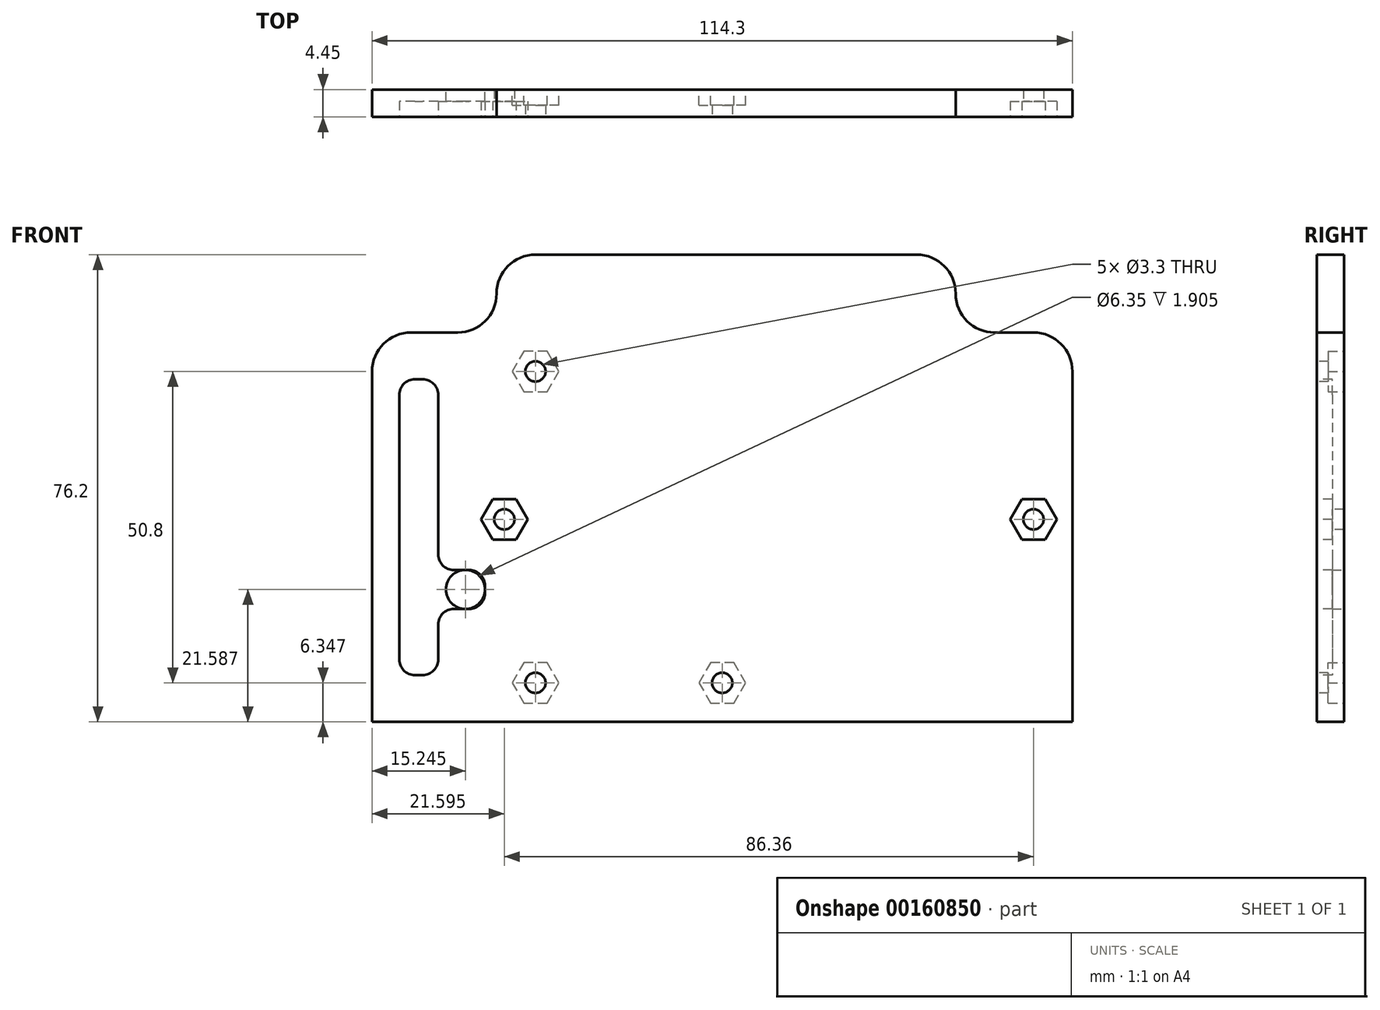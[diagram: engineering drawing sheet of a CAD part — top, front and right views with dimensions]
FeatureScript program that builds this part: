
annotation { "Feature Type Name" : "Feature", "Feature Type Description" : "" }
export const myFeature = defineFeature(function(context is Context, id is Id, definition is map)
    precondition{}
    {
        {
            var Q0;
            Q0=qCreatedBy(makeId("Front.planeOp"),FACE);
            var sketch = newSketch(context, id + "F0", { "sketchPlane" : qUnion([Q0])});
            skLineSegment(sketch, "E0.bottom", {"start": v(-28.43, 40.82) * mm, "end": v(33.8, 40.82) * mm});
            skLineSegment(sketch, "E0.top", {"start": v(-55.1, -35.38) * mm, "end": v(59.2, -35.38) * mm});
            skLineSegment(sketch, "E0.left", {"start": v(-55.1, 21.77) * mm, "end": v(-55.1, -35.38) * mm});
            skLineSegment(sketch, "E0.right", {"start": v(59.2, 21.77) * mm, "end": v(59.2, -35.38) * mm});
            skLineSegment(sketch, "E1.top", {"start": v(-48.75, 28.12) * mm, "end": v(-41.13, 28.12) * mm});
            skLineSegment(sketch, "E1.right", {"start": v(-34.78, 34.47) * mm, "end": v(-34.78, 34.47) * mm});
            skPoint(sketch, "E2.visualSharp", {"position": v(-55.1, 28.12) * mm});
            skArc(sketch, "E2.filletArc", {"start": v(-48.75, 28.12) * mm, "mid": v(-53.24, 26.26) * mm, "end": v(-55.1, 21.77) * mm});
            skPoint(sketch, "E3.visualSharp", {"position": v(-34.78, 40.82) * mm});
            skArc(sketch, "E3.filletArc", {"start": v(-28.43, 40.82) * mm, "mid": v(-32.92, 38.96) * mm, "end": v(-34.78, 34.47) * mm});
            skPoint(sketch, "E4.visualSharp", {"position": v(59.2, 40.82) * mm});
            skLineSegment(sketch, "E5.top", {"start": v(46.5, 28.12) * mm, "end": v(52.85, 28.12) * mm});
            skLineSegment(sketch, "E5.left", {"start": v(40.15, 34.47) * mm, "end": v(40.15, 34.47) * mm});
            skPoint(sketch, "E6.visualSharp", {"position": v(40.15, 28.12) * mm});
            skArc(sketch, "E6.filletArc", {"start": v(40.15, 34.47) * mm, "mid": v(42.01, 29.98) * mm, "end": v(46.5, 28.12) * mm});
            skPoint(sketch, "E7.visualSharp", {"position": v(40.15, 40.82) * mm});
            skArc(sketch, "E7.filletArc", {"start": v(40.15, 34.47) * mm, "mid": v(38.3, 38.96) * mm, "end": v(33.8, 40.82) * mm});
            skPoint(sketch, "E8.visualSharp", {"position": v(59.2, 28.12) * mm});
            skArc(sketch, "E8.filletArc", {"start": v(59.2, 21.77) * mm, "mid": v(57.34, 26.26) * mm, "end": v(52.85, 28.12) * mm});
            skPoint(sketch, "E9.visualSharp", {"position": v(-34.78, 28.12) * mm});
            skArc(sketch, "E9.filletArc", {"start": v(-41.13, 28.12) * mm, "mid": v(-36.64, 29.98) * mm, "end": v(-34.78, 34.47) * mm});
            skSolve(sketch);
        }
        {
            var Q0;
            Q0 = qSketchRegion(id + "F0", true);
            extrude(context, id + "F1", {"entities" : qUnion([Q0]), "depth" : 4.44 * mm});
        }
        {
            var Q0;
            Q0=makeQuery(id+"F1.opExtrude","CAP_FACE",FACE,{"disambiguationData":[OSD([sQuery(id+"F0.wireOp",EDGE,"E0.bottom"),sQuery(id+"F0.wireOp",EDGE,"E0.top"),sQuery(id+"F0.wireOp",EDGE,"E0.left"),sQuery(id+"F0.wireOp",EDGE,"E0.right"),sQuery(id+"F0.wireOp",EDGE,"E1.top"),sQuery(id+"F0.wireOp",EDGE,"E1.right"),sQuery(id+"F0.wireOp",EDGE,"E2.filletArc"),sQuery(id+"F0.wireOp",EDGE,"E3.filletArc"),sQuery(id+"F0.wireOp",EDGE,"E4.filletArc")])],"isStart":false});
            var sketch = newSketch(context, id + "F2", { "sketchPlane" : qUnion([Q0])});
            skCircle(sketch, "E10", {"center": v(-28.43, -29.03) * mm, "radius": 1.65 * mm});
            skCircle(sketch, "E11", {"center": v(2.05, -29.03) * mm, "radius": 1.65 * mm});
            skCircle(sketch, "E12", {"center": v(-28.43, 21.77) * mm, "radius": 1.65 * mm});
            skSolve(sketch);
        }
        {
            var Q0;
            Q0 = qSketchRegion(id + "F2", true);
            extrude(context, id + "F3", {"entities" : qUnion([Q0]), "operationType" : NewBodyOperationType.REMOVE, "endBound" : BoundingType.THROUGH_ALL, "oppositeDirection" : true, "depth" : 25.4 * mm});
        }
        {
            var Q0;
            Q0=makeQuery(id+"F1.opExtrude","CAP_FACE",FACE,{"disambiguationData":[OSD([sQuery(id+"F0.wireOp",EDGE,"E0.bottom"),sQuery(id+"F0.wireOp",EDGE,"E0.top"),sQuery(id+"F0.wireOp",EDGE,"E0.left"),sQuery(id+"F0.wireOp",EDGE,"E0.right"),sQuery(id+"F0.wireOp",EDGE,"E1.top"),sQuery(id+"F0.wireOp",EDGE,"E1.right"),sQuery(id+"F0.wireOp",EDGE,"E2.filletArc"),sQuery(id+"F0.wireOp",EDGE,"E3.filletArc"),sQuery(id+"F0.wireOp",EDGE,"E4.filletArc")])],"isStart":false});
            var sketch = newSketch(context, id + "F4", { "sketchPlane" : qUnion([Q0])});
            skCircle(sketch, "E13", {"center": v(-33.5, -2.36) * mm, "radius": 1.65 * mm});
            skCircle(sketch, "E14", {"center": v(52.85, -2.36) * mm, "radius": 1.65 * mm});
            skSolve(sketch);
        }
        {
            var Q0;
            Q0 = qSketchRegion(id + "F4", true);
            extrude(context, id + "F5", {"entities" : qUnion([Q0]), "operationType" : NewBodyOperationType.REMOVE, "endBound" : BoundingType.THROUGH_ALL, "oppositeDirection" : true, "depth" : 25.4 * mm});
        }
        {
            var Q0;
            Q0=makeQuery(id+"F1.opExtrude","CAP_FACE",FACE,{"disambiguationData":[OSD([sQuery(id+"F0.wireOp",EDGE,"E0.bottom"),sQuery(id+"F0.wireOp",EDGE,"E0.top"),sQuery(id+"F0.wireOp",EDGE,"E0.left"),sQuery(id+"F0.wireOp",EDGE,"E0.right"),sQuery(id+"F0.wireOp",EDGE,"E1.top"),sQuery(id+"F0.wireOp",EDGE,"E1.right"),sQuery(id+"F0.wireOp",EDGE,"E2.filletArc"),sQuery(id+"F0.wireOp",EDGE,"E3.filletArc"),sQuery(id+"F0.wireOp",EDGE,"E4.filletArc")])],"isStart":false});
            var sketch = newSketch(context, id + "F6", { "sketchPlane" : qUnion([Q0])});
            skCircle(sketch, "E15.cCircle", {"center": v(-33.5, -2.36) * mm, "radius": 3.81 * mm, "construction": true});
            skLineSegment(sketch, "E15.0", {"start": v(-31.6, 0.94) * mm, "end": v(-29.7, -2.36) * mm});
            skLineSegment(sketch, "E15.1", {"start": v(-29.7, -2.36) * mm, "end": v(-31.6, -5.66) * mm});
            skLineSegment(sketch, "E15.2", {"start": v(-31.6, -5.66) * mm, "end": v(-35.41, -5.66) * mm});
            skLineSegment(sketch, "E15.3", {"start": v(-35.41, -5.66) * mm, "end": v(-37.32, -2.36) * mm});
            skLineSegment(sketch, "E15.4", {"start": v(-37.32, -2.36) * mm, "end": v(-35.41, 0.94) * mm});
            skLineSegment(sketch, "E15.5", {"start": v(-35.41, 0.94) * mm, "end": v(-31.6, 0.94) * mm});
            skCircle(sketch, "E16.cCircle", {"center": v(52.85, -2.36) * mm, "radius": 3.81 * mm, "construction": true});
            skLineSegment(sketch, "E16.0", {"start": v(50.95, 0.94) * mm, "end": v(54.76, 0.94) * mm});
            skLineSegment(sketch, "E16.1", {"start": v(54.76, 0.94) * mm, "end": v(56.66, -2.36) * mm});
            skLineSegment(sketch, "E16.2", {"start": v(56.66, -2.36) * mm, "end": v(54.76, -5.66) * mm});
            skLineSegment(sketch, "E16.3", {"start": v(54.76, -5.66) * mm, "end": v(50.95, -5.66) * mm});
            skLineSegment(sketch, "E16.4", {"start": v(50.95, -5.66) * mm, "end": v(49.04, -2.36) * mm});
            skLineSegment(sketch, "E16.5", {"start": v(49.04, -2.36) * mm, "end": v(50.95, 0.94) * mm});
            skSolve(sketch);
        }
        {
            var Q0;
            Q0 = qSketchRegion(id + "F6", true);
            extrude(context, id + "F7", {"entities" : qUnion([Q0]), "operationType" : NewBodyOperationType.REMOVE, "oppositeDirection" : true, "depth" : 2.54 * mm});
        }
        {
            var Q0;
            Q0=makeQuery(id+"F1.opExtrude","CAP_FACE",FACE,{"disambiguationData":[OSD([sQuery(id+"F0.wireOp",EDGE,"E0.bottom"),sQuery(id+"F0.wireOp",EDGE,"E0.top"),sQuery(id+"F0.wireOp",EDGE,"E0.left"),sQuery(id+"F0.wireOp",EDGE,"E0.right"),sQuery(id+"F0.wireOp",EDGE,"E1.top"),sQuery(id+"F0.wireOp",EDGE,"E1.right"),sQuery(id+"F0.wireOp",EDGE,"E2.filletArc"),sQuery(id+"F0.wireOp",EDGE,"E3.filletArc"),sQuery(id+"F0.wireOp",EDGE,"E4.filletArc")])],"isStart":true});
            var sketch = newSketch(context, id + "F8", { "sketchPlane" : qUnion([Q0])});
            skCircle(sketch, "E17.cCircle", {"center": v(28.43, 21.77) * mm, "radius": 3.81 * mm, "construction": true});
            skLineSegment(sketch, "E17.0", {"start": v(32.24, 21.77) * mm, "end": v(30.33, 18.47) * mm});
            skLineSegment(sketch, "E17.1", {"start": v(30.33, 18.47) * mm, "end": v(26.52, 18.47) * mm});
            skLineSegment(sketch, "E17.2", {"start": v(26.52, 18.47) * mm, "end": v(24.62, 21.77) * mm});
            skLineSegment(sketch, "E17.3", {"start": v(24.62, 21.77) * mm, "end": v(26.52, 25.07) * mm});
            skLineSegment(sketch, "E17.4", {"start": v(26.52, 25.07) * mm, "end": v(30.33, 25.07) * mm});
            skLineSegment(sketch, "E17.5", {"start": v(30.33, 25.07) * mm, "end": v(32.24, 21.77) * mm});
            skCircle(sketch, "E18.cCircle", {"center": v(28.43, -29.03) * mm, "radius": 3.8 * mm, "construction": true});
            skLineSegment(sketch, "E18.0", {"start": v(30.33, -25.73) * mm, "end": v(32.24, -29.03) * mm});
            skLineSegment(sketch, "E18.1", {"start": v(32.24, -29.03) * mm, "end": v(30.33, -32.33) * mm});
            skLineSegment(sketch, "E18.2", {"start": v(30.33, -32.33) * mm, "end": v(26.52, -32.33) * mm});
            skLineSegment(sketch, "E18.3", {"start": v(26.52, -32.33) * mm, "end": v(24.62, -29.03) * mm});
            skLineSegment(sketch, "E18.4", {"start": v(24.62, -29.03) * mm, "end": v(26.52, -25.73) * mm});
            skLineSegment(sketch, "E18.5", {"start": v(26.52, -25.73) * mm, "end": v(30.33, -25.73) * mm});
            skCircle(sketch, "E19.cCircle", {"center": v(-2.05, -29.03) * mm, "radius": 3.8 * mm, "construction": true});
            skLineSegment(sketch, "E19.0", {"start": v(-3.96, -25.73) * mm, "end": v(-0.15, -25.73) * mm});
            skLineSegment(sketch, "E19.1", {"start": v(-0.15, -25.73) * mm, "end": v(1.76, -29.03) * mm});
            skLineSegment(sketch, "E19.2", {"start": v(1.76, -29.03) * mm, "end": v(-0.15, -32.33) * mm});
            skLineSegment(sketch, "E19.3", {"start": v(-0.15, -32.33) * mm, "end": v(-3.96, -32.33) * mm});
            skLineSegment(sketch, "E19.4", {"start": v(-3.96, -32.33) * mm, "end": v(-5.86, -29.03) * mm});
            skLineSegment(sketch, "E19.5", {"start": v(-5.86, -29.03) * mm, "end": v(-3.96, -25.73) * mm});
            skSolve(sketch);
        }
        {
            var Q0;
            Q0 = qSketchRegion(id + "F8", true);
            extrude(context, id + "F9", {"entities" : qUnion([Q0]), "operationType" : NewBodyOperationType.REMOVE, "oppositeDirection" : true, "depth" : 2.54 * mm});
        }
        {
            var Q0;
            Q0=makeQuery(id+"F1.opExtrude","CAP_FACE",FACE,{"disambiguationData":[OSD([sQuery(id+"F0.wireOp",EDGE,"E0.bottom"),sQuery(id+"F0.wireOp",EDGE,"E0.top"),sQuery(id+"F0.wireOp",EDGE,"E0.left"),sQuery(id+"F0.wireOp",EDGE,"E0.right"),sQuery(id+"F0.wireOp",EDGE,"E1.top"),sQuery(id+"F0.wireOp",EDGE,"E1.right"),sQuery(id+"F0.wireOp",EDGE,"E2.filletArc"),sQuery(id+"F0.wireOp",EDGE,"E3.filletArc"),sQuery(id+"F0.wireOp",EDGE,"E4.filletArc")])],"isStart":true});
            var sketch = newSketch(context, id + "F10", { "sketchPlane" : qUnion([Q0])});
            skCircle(sketch, "E20", {"center": v(39.86, -13.8) * mm, "radius": 3.18 * mm});
            skSolve(sketch);
        }
        {
            var Q0;
            Q0 = qSketchRegion(id + "F10", true);
            extrude(context, id + "F11", {"entities" : qUnion([Q0]), "operationType" : NewBodyOperationType.REMOVE, "endBound" : BoundingType.THROUGH_ALL, "oppositeDirection" : true, "depth" : 25.4 * mm});
        }
        {
            var Q0;
            Q0=makeQuery(id+"F1.opExtrude","CAP_FACE",FACE,{"disambiguationData":[OSD([sQuery(id+"F0.wireOp",EDGE,"E0.bottom"),sQuery(id+"F0.wireOp",EDGE,"E0.top"),sQuery(id+"F0.wireOp",EDGE,"E0.left"),sQuery(id+"F0.wireOp",EDGE,"E0.right"),sQuery(id+"F0.wireOp",EDGE,"E1.top"),sQuery(id+"F0.wireOp",EDGE,"E1.right"),sQuery(id+"F0.wireOp",EDGE,"E2.filletArc"),sQuery(id+"F0.wireOp",EDGE,"E3.filletArc"),sQuery(id+"F0.wireOp",EDGE,"E4.filletArc")])],"isStart":false});
            var sketch = newSketch(context, id + "F12", { "sketchPlane" : qUnion([Q0])});
            skLineSegment(sketch, "E21.bottom", {"start": v(-48.11, 20.5) * mm, "end": v(-46.84, 20.5) * mm});
            skLineSegment(sketch, "E21.top", {"start": v(-48.11, -27.76) * mm, "end": v(-46.84, -27.76) * mm});
            skLineSegment(sketch, "E21.left", {"start": v(-50.65, 17.96) * mm, "end": v(-50.65, -25.22) * mm});
            skLineSegment(sketch, "E21.right", {"start": v(-44.3, 17.96) * mm, "end": v(-44.3, -8.08) * mm});
            skPoint(sketch, "E22.visualSharp", {"position": v(-50.65, 20.5) * mm});
            skArc(sketch, "E22.filletArc", {"start": v(-48.11, 20.5) * mm, "mid": v(-49.9, 19.75) * mm, "end": v(-50.65, 17.96) * mm});
            skPoint(sketch, "E23.visualSharp", {"position": v(-44.3, 20.5) * mm});
            skArc(sketch, "E23.filletArc", {"start": v(-44.3, 17.96) * mm, "mid": v(-45.04, 19.75) * mm, "end": v(-46.84, 20.5) * mm});
            skPoint(sketch, "E24.visualSharp", {"position": v(-44.3, -27.76) * mm});
            skArc(sketch, "E24.filletArc", {"start": v(-46.84, -27.76) * mm, "mid": v(-45.04, -27.02) * mm, "end": v(-44.3, -25.22) * mm});
            skPoint(sketch, "E25.visualSharp", {"position": v(-50.65, -27.76) * mm});
            skArc(sketch, "E25.filletArc", {"start": v(-50.65, -25.22) * mm, "mid": v(-49.9, -27.02) * mm, "end": v(-48.11, -27.76) * mm});
            skLineSegment(sketch, "E26.bottom", {"start": v(-41.76, -10.62) * mm, "end": v(-39.22, -10.62) * mm});
            skLineSegment(sketch, "E26.top", {"start": v(-41.76, -16.97) * mm, "end": v(-39.22, -16.97) * mm});
            skLineSegment(sketch, "E26.left", {"start": v(-50.65, -10.62) * mm, "end": v(-50.65, -16.97) * mm});
            skLineSegment(sketch, "E26.right", {"start": v(-36.68, -13.16) * mm, "end": v(-36.68, -14.43) * mm});
            skLineSegment(sketch, "E27.trimOffspring", {"start": v(-44.3, -19.5) * mm, "end": v(-44.3, -25.22) * mm});
            skPoint(sketch, "E28.visualSharp", {"position": v(-36.68, -10.62) * mm});
            skArc(sketch, "E28.filletArc", {"start": v(-36.68, -13.16) * mm, "mid": v(-37.42, -11.36) * mm, "end": v(-39.22, -10.62) * mm});
            skPoint(sketch, "E29.visualSharp", {"position": v(-36.68, -16.97) * mm});
            skArc(sketch, "E29.filletArc", {"start": v(-39.22, -16.97) * mm, "mid": v(-37.42, -16.22) * mm, "end": v(-36.68, -14.43) * mm});
            skPoint(sketch, "E30.visualSharp", {"position": v(-44.3, -16.97) * mm});
            skArc(sketch, "E30.filletArc", {"start": v(-41.76, -16.97) * mm, "mid": v(-43.56, -17.71) * mm, "end": v(-44.3, -19.5) * mm});
            skPoint(sketch, "E31.visualSharp", {"position": v(-44.3, -10.62) * mm});
            skArc(sketch, "E31.filletArc", {"start": v(-44.3, -8.08) * mm, "mid": v(-43.56, -9.87) * mm, "end": v(-41.76, -10.62) * mm});
            skSolve(sketch);
        }
        {
            var Q0;
            Q0 = qSketchRegion(id + "F12", true);
            extrude(context, id + "F13", {"entities" : qUnion([Q0]), "operationType" : NewBodyOperationType.REMOVE, "oppositeDirection" : true, "depth" : 2.54 * mm});
        }
    });
